# Revit family: PRD_FrankeWS_WlHngWshBsns_AnimaWashbasin_ANMX500,501,600,601
name_source: partatom
category: Plumbing Fixtures
revit_build: Autodesk Revit 2018 (Build: 20190510_1515(x64)
units: mm (PartAtom-declared; Revit-internal decimal feet)

## family parameters
Cut with Voids When Loaded = No
Host = Face
OmniClass Number = 23.45.05.14.14
OmniClass Title = Sinks/Lavatories
Part Type = Normal
Room Calculation Point = No
Round Connector Dimension = Use Diameter
Shared = No

## types (4) — shared parameters
AssetType = Fixed
Category = Pr_40_20_96_96, Wall-hung wash basins
Color = Stainless steel
Default Elevation = 850 mm  [stored 2.78871 ft]
DrainSize = DN 32 (1 1/4 inch.)
DurationUnit = year
Finish = Satin finished
Form = Wall hung wash basin
IfcExportAs = IfcSanitaryTerminalType
IfcExportType = WASHHANDBASIN
IntegralAccessories = Incl. stainless steel screws and dowels
Manufacturer = KWC Group AG
ManufacturerName = KWC Group AG
ManufacturerURL = www.kwc.com
Material = Stainless steel
MaterialsBody = Stainless steel 1.4301
MaterialsFinishAndColour = Stainless steel, satin finished
NBSDescription = Wall hung wash basins
NBSReference = 45-35-70/369
NominalDepth = 500 mm  [stored 1.64042 ft]
NominalHeight = 160 mm  [stored 0.524934 ft]
ProductInformation = https://pim.kwc.com
Shape = Rectangular
URL = www.kwc.com
Uniclass2015Code = Pr_40_20_96_96
Uniclass2015Title = Wall-hung wash basins
Uniclass2015Version = Products v1.10
Version = 1
WarrantyDurationUnit = year
WashHandBasinMounting = WallHung
WashHandBasinType = HandRinse
WashbasinMaterial = PRD_AR_StainlessSteel_SatinFinished
WasteSize = 32
WaterSupplyOverflowAndWasteHolesOverflow = None
WaterSupplyOverflowAndWasteHolesWaste = Center-Center

## per-type parameters (varying)
| type | BIMObjectName | Description | Features | GrossWeight | Model | ModelNumber | ModelReference | Name | NetWeight | NominalWidth | Size | Taphole | Type | WaterSupplyOverflowAndWasteHolesWaterSupply |
| ANMX500 - without taphole | PRD_AR_WallHungWashBasins_AnimaWashbasin_ANMX500 | Wash basin for disabled for wall mounting, stainless steel, surface satin finished, material thickness 1.2 mm, seamless welded round bowl with diameter 350 mm, rectangular shape, 75 mm tap ledge, without overflow, seamless welded waste with 32 mm drain pipe, drainage centric, prewelded mounting brackets, for recessed trap mounting - trap not included, mounting conform to EN 31, disabled accessible mounting possible, incl. stainless steel screws and dowels. width 500 mm, without taphole | stainless steel, 1.20 mm, satin finished, wall mounting, 500x160x500 mm (WxHxD) | 10.20 kg | ANMX500 | 2000056724 | ANMX500 | ANIMA wall-hung wash basin ANMX500 | 9.00 kg | 500 mm  [stored 1.64042 ft] | 500 x 500 x 160 mm | No | ANMX500 | No tapholes |
| ANMX501 - with taphole | PRD_AR_WallHungWashBasins_AnimaWashbasin_ANMX501 | Wash basin for disabled for wall mounting, stainless steel, surface satin finished, material thickness 1.2 mm, seamless welded round bowl with diameter 350 mm, rectangular shape, 75 mm tap ledge, without overflow, seamless welded waste with 32 mm drain pipe, drainage centric, prewelded mounting brackets, for recessed trap mounting - trap not included, mounting conform to EN 31, disabled accessible mounting possible, incl. stainless steel screws and dowels. width 500 mm, with taphole, centered | stainless steel, 1.20 mm, satin finished, wall mounting, 500x160x500 mm (WxHxD) | 10.40 kg | ANMX501 | 2000056774 | ANMX501 | ANIMA wall-hung wash basin ANMX501 | 9.20 kg | 500 mm  [stored 1.64042 ft] | 500 x 500 x 160 mm | Yes | ANMX500 | Single tap hole, middle, 35 mm |
| ANMX600 - without taphole | PRD_AR_WallHungWashBasins_AnimaWashbasin_ANMX600 | Wash basin for disabled for wall mounting, stainless steel, surface satin finished, material thickness 1.2 mm, seamless welded round bowl with diameter 350 mm, rectangular shape, 75 mm tap ledge, without overflow, seamless welded waste with 32 mm drain pipe, drainage centric, prewelded mounting brackets, for recessed trap mounting - trap not included, mounting conform to EN 31, disabled accessible mounting possible, incl. stainless steel screws and dowels. width 600 mm, without taphole | stainless steel, 1.20 mm, satin finished, wall mounting, 600x160x500 mm (WxHxD) | 13.60 kg | ANMX600 | 2000100022 | ANMX600 | ANIMA wall-hung wash basin ANMX600 | 11.50 kg | 600 mm | 600 x 500 x 160 mm | No | ANMX600 | No tapholes |
| ANMX601 - with taphole | PRD_AR_WallHungWashBasins_AnimaWashbasin_ANMX601 | Wash basin for disabled for wall mounting, stainless steel, surface satin finished, material thickness 1.2 mm, seamless welded round bowl with diameter 350 mm, rectangular shape, 75 mm tap ledge, without overflow, seamless welded waste with 32 mm drain pipe, drainage centric, prewelded mounting brackets, for recessed trap mounting - trap not included, mounting conform to EN 31, disabled accessible mounting possible, incl. stainless steel screws and dowels. width 600 mm, with taphole, centered | stainless steel, 1.20 mm, satin finished, wall mounting, 600x160x500 mm (WxHxD) | 13.80 kg | ANMX601 | 2000100023 | ANMX601 | ANIMA wall-hung wash basin ANMX601 | 12.00 kg | 600 mm | 600 x 500 x 160 mm | Yes | ANMX600 | Single tap hole, middle, 35 mm |

note: [stored X ft] marks values corroborated as IEEE doubles in the binary element streams (Revit-internal decimal feet)

## geometry (parser evidence)
native form markers: Sweep x8
no freeform markers — native parametric forms only
